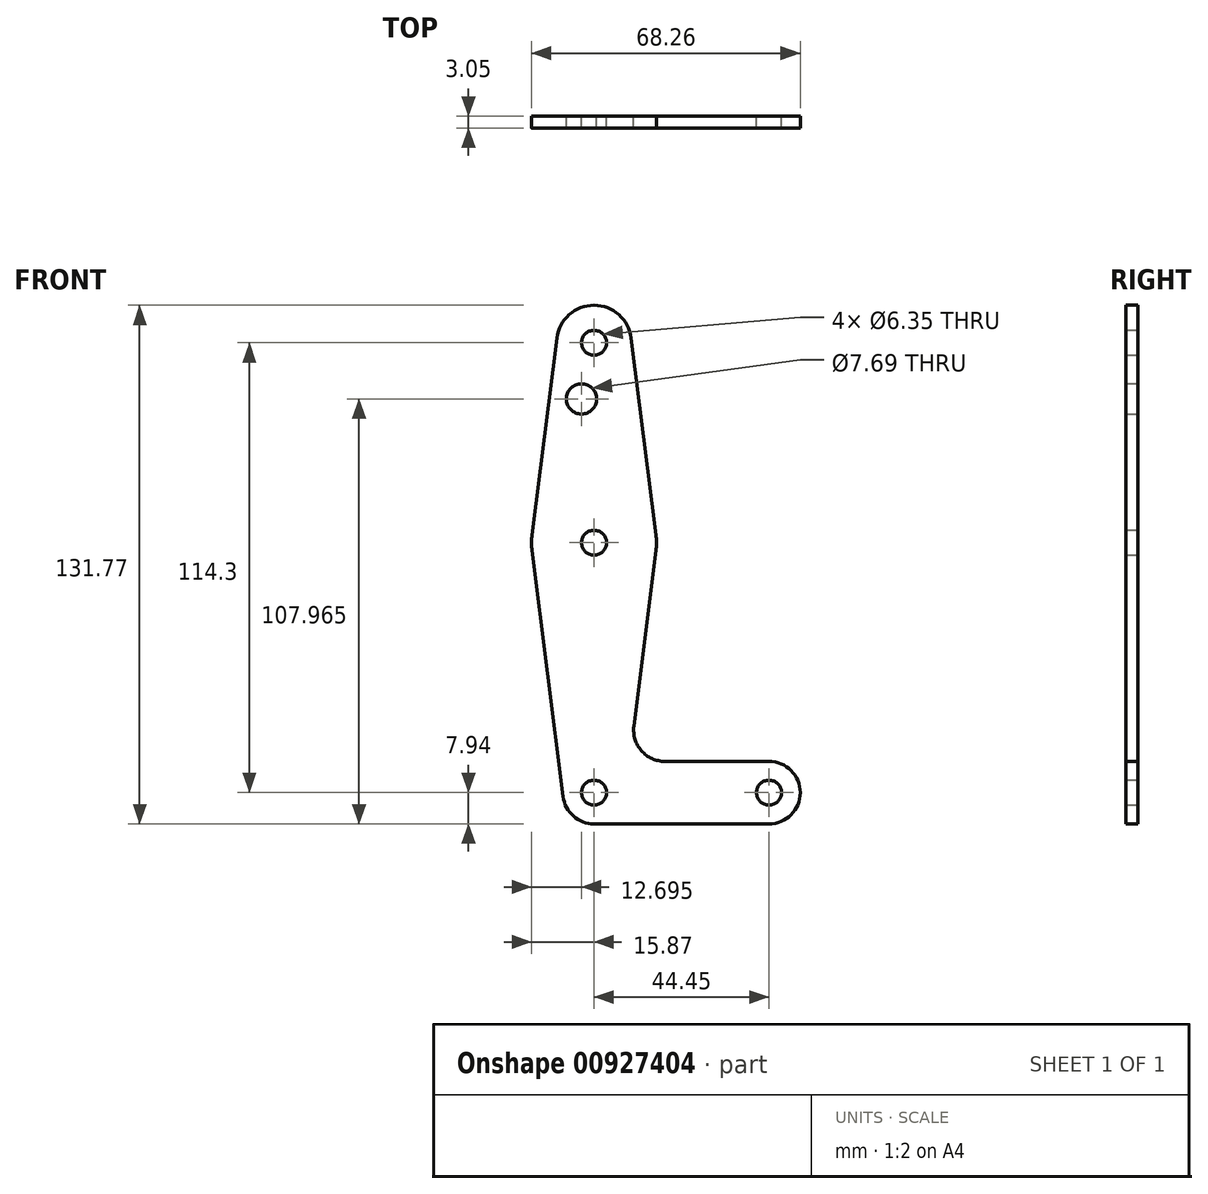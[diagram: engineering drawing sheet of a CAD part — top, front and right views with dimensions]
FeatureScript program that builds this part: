
annotation { "Feature Type Name" : "Feature", "Feature Type Description" : "" }
export const myFeature = defineFeature(function(context is Context, id is Id, definition is map)
    precondition{}
    {
        {
            var Q0;
            Q0=qCreatedBy(makeId("Front.planeOp"),FACE);
            var sketch = newSketch(context, id + "F0", { "sketchPlane" : qUnion([Q0])});
            skLineSegment(sketch, "E0", {"start": v(0, 0) * mm, "end": v(0, 114.3) * mm});
            skLineSegment(sketch, "E1", {"start": v(0, 0) * mm, "end": v(44.45, 0) * mm});
            skCircle(sketch, "E2", {"center": v(0, 114.3) * mm, "radius": 9.53 * mm});
            skCircle(sketch, "E3", {"center": v(0, 63.5) * mm, "radius": 15.88 * mm});
            skCircle(sketch, "E4", {"center": v(0, 0) * mm, "radius": 7.94 * mm});
            skCircle(sketch, "E5", {"center": v(44.45, 0) * mm, "radius": 7.94 * mm});
            skLineSegment(sketch, "E6", {"start": v(9.45, 115.5) * mm, "end": v(15.75, 65.48) * mm});
            skLineSegment(sketch, "E7", {"start": v(-9.45, 115.5) * mm, "end": v(-15.75, 65.48) * mm});
            skLineSegment(sketch, "E8", {"start": v(-15.75, 61.52) * mm, "end": v(-7.88, -1) * mm});
            skLineSegment(sketch, "E9", {"start": v(15.75, 61.52) * mm, "end": v(10.13, 16.88) * mm});
            skLineSegment(sketch, "E10", {"start": v(18.01, 7.94) * mm, "end": v(44.45, 7.94) * mm});
            skLineSegment(sketch, "E11", {"start": v(0, -7.94) * mm, "end": v(44.45, -7.94) * mm});
            skCircle(sketch, "E12", {"center": v(0, 114.3) * mm, "radius": 3.18 * mm});
            skCircle(sketch, "E13", {"center": v(0, 63.5) * mm, "radius": 3.18 * mm});
            skCircle(sketch, "E14", {"center": v(0, 0) * mm, "radius": 3.18 * mm});
            skCircle(sketch, "E15", {"center": v(44.45, 0) * mm, "radius": 3.18 * mm});
            skCircle(sketch, "E16", {"center": v(-3.18, 100.03) * mm, "radius": 3.85 * mm});
            skArc(sketch, "E17.filletArc", {"start": v(10.13, 16.88) * mm, "mid": v(12.05, 10.63) * mm, "end": v(18.01, 7.94) * mm});
            skSolve(sketch);
        }
        {
            var Q0;
            Q0=makeQuery(id+"F0.imprint","IMPRINT",FACE,{"disambiguationData":[TD([[makeQuery(id+"F0.imprint","IMPRINT",EDGE,{"derivedFrom":sQuery(id+"F0.wireOp",EDGE,"E12")}),-1.0]])]});
            var Q1;
            {var subQ0=sQuery(id+"F0.wireOp",EDGE,"E7");Q1=makeQuery(id+"F0.imprint","IMPRINT",FACE,{"disambiguationData":[TD([[makeQuery(id+"F0.imprint","IMPRINT",EDGE,{"derivedFrom":subQ0}),1.0]])]});}
            var Q2;
            {var subQ0=sQuery(id+"F0.wireOp",EDGE,"E6");Q2=makeQuery(id+"F0.imprint","IMPRINT",FACE,{"disambiguationData":[TD([[makeQuery(id+"F0.imprint","IMPRINT",EDGE,{"derivedFrom":subQ0}),-1.0]])]});}
            var Q3;
            {var subQ0=sQuery(id+"F0.wireOp",EDGE,"E9");Q3=makeQuery(id+"F0.imprint","IMPRINT",FACE,{"disambiguationData":[TD([[makeQuery(id+"F0.imprint","IMPRINT",EDGE,{"derivedFrom":subQ0}),-1.0]])]});}
            var Q4;
            {var subQ0=sQuery(id+"F0.wireOp",EDGE,"E3");var subQ2=sQuery(id+"F0.wireOp",EDGE,"E0");var subQ3=makeQuery(id+"F0.imprint","INTERSECT",VERTEX,{"disambiguationData":[OD(0.0)],"derivedFrom":[subQ2,subQ0]});Q4=makeQuery(id+"F0.imprint","IMPRINT",FACE,{"disambiguationData":[TD([[makeQuery(id+"F0.imprint","IMPRINT",EDGE,{"disambiguationData":[TD([[subQ3,-1.0]])],"derivedFrom":subQ2}),-1.0]])]});}
            var Q5;
            {var subQ0=sQuery(id+"F0.wireOp",EDGE,"E3");var subQ3=sQuery(id+"F0.wireOp",EDGE,"E0");var subQ7=makeQuery(id+"F0.imprint","INTERSECT",VERTEX,{"disambiguationData":[OD(0.0)],"derivedFrom":[subQ3,subQ0]});Q5=makeQuery(id+"F0.imprint","IMPRINT",FACE,{"disambiguationData":[TD([[makeQuery(id+"F0.imprint","IMPRINT",EDGE,{"disambiguationData":[TD([[subQ7,-1.0]])],"derivedFrom":subQ3}),1.0]])]});}
            var Q6;
            {var subQ5=sQuery(id+"F0.wireOp",EDGE,"E8");Q6=makeQuery(id+"F0.imprint","IMPRINT",FACE,{"disambiguationData":[TD([[makeQuery(id+"F0.imprint","IMPRINT",EDGE,{"derivedFrom":subQ5}),1.0]])]});}
            var Q7;
            {var subQ5=sQuery(id+"F0.wireOp",EDGE,"E11");Q7=makeQuery(id+"F0.imprint","IMPRINT",FACE,{"disambiguationData":[TD([[makeQuery(id+"F0.imprint","IMPRINT",EDGE,{"derivedFrom":subQ5}),1.0]])]});}
            var Q8;
            Q8=makeQuery(id+"F0.imprint","IMPRINT",FACE,{"disambiguationData":[TD([[makeQuery(id+"F0.imprint","IMPRINT",EDGE,{"derivedFrom":sQuery(id+"F0.wireOp",EDGE,"E15")}),-1.0]])]});
            var Q9;
            {var subQ3=sQuery(id+"F0.wireOp",EDGE,"E14");var subQ4=sQuery(id+"F0.wireOp",EDGE,"E0");var subQ5=makeQuery(id+"F0.imprint","INTERSECT",VERTEX,{"derivedFrom":[subQ4,subQ3]});Q9=makeQuery(id+"F0.imprint","IMPRINT",FACE,{"disambiguationData":[TD([[makeQuery(id+"F0.imprint","IMPRINT",EDGE,{"disambiguationData":[TD([[subQ5,-1.0]])],"derivedFrom":subQ4}),1.0]])]});}
            var Q10;
            {var subQ0=sQuery(id+"F0.wireOp",EDGE,"E14");var subQ1=sQuery(id+"F0.wireOp",EDGE,"E0");var subQ2=makeQuery(id+"F0.imprint","INTERSECT",VERTEX,{"derivedFrom":[subQ1,subQ0]});Q10=makeQuery(id+"F0.imprint","IMPRINT",FACE,{"disambiguationData":[TD([[makeQuery(id+"F0.imprint","IMPRINT",EDGE,{"disambiguationData":[TD([[subQ2,-1.0]])],"derivedFrom":subQ1}),-1.0]])]});}
            extrude(context, id + "F1", {"entities" : qUnion([Q0, Q1, Q2, Q3, Q4, Q5, Q6, Q7, Q8, Q9, Q10]), "depth" : 3.05 * mm, "offsetDistance" : 25.4 * mm});
        }
    });
